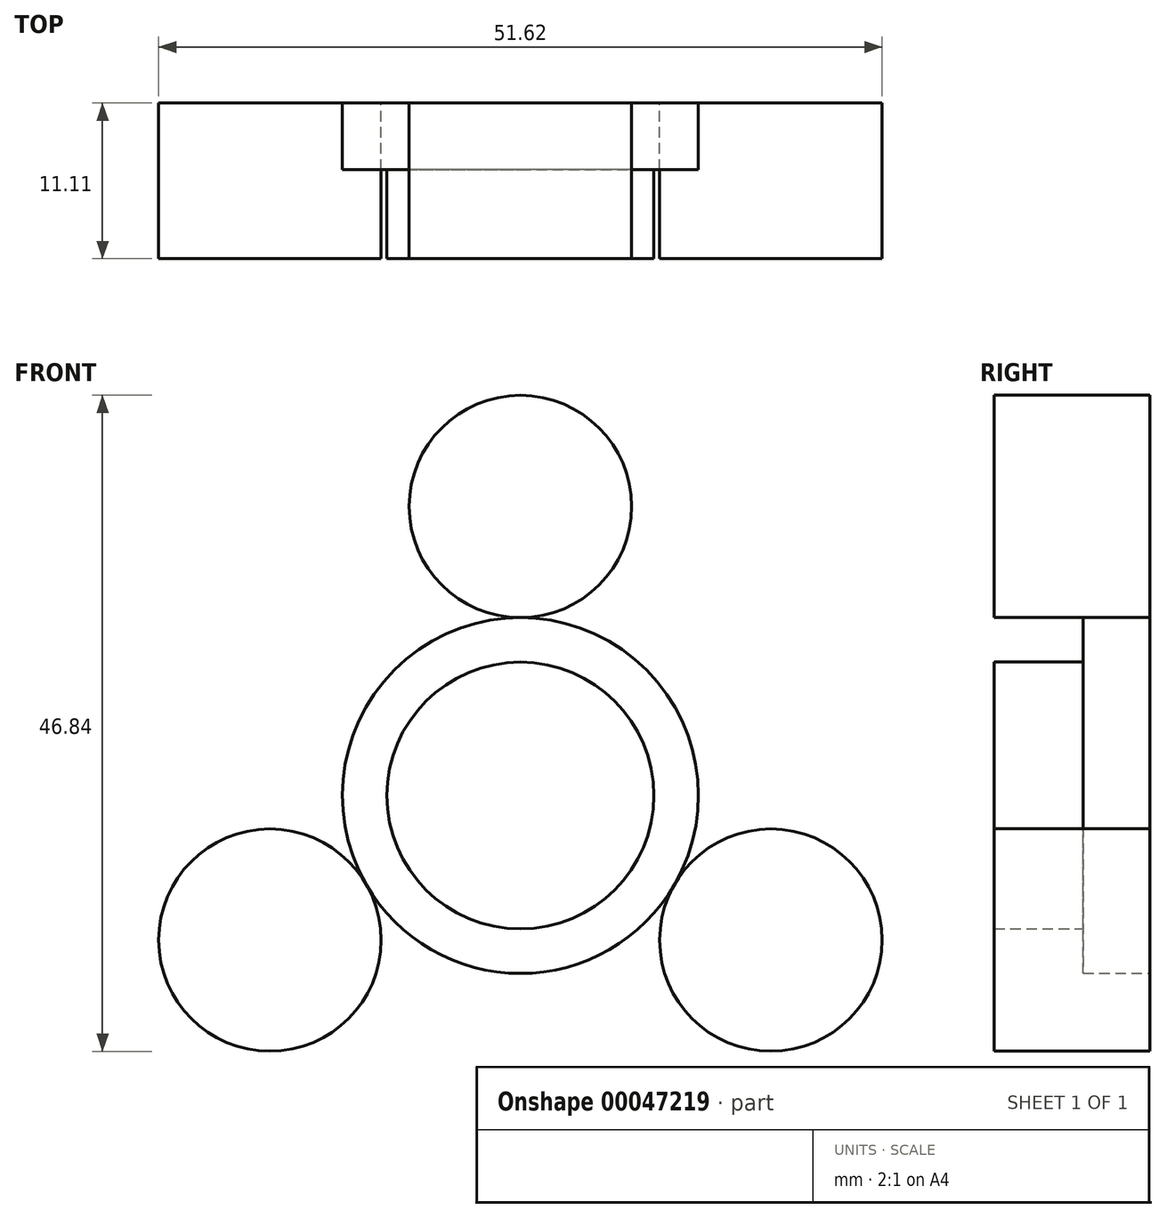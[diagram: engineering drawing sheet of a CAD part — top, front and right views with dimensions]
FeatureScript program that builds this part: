
annotation { "Feature Type Name" : "Feature", "Feature Type Description" : "" }
export const myFeature = defineFeature(function(context is Context, id is Id, definition is map)
    precondition{}
    {
        {
            var Q0;
            Q0=qCreatedBy(makeId("Front.planeOp"),FACE);
            var sketch = newSketch(context, id + "F0", { "sketchPlane" : qUnion([Q0])});
            skCircle(sketch, "E0", {"center": v(0, 0) * mm, "radius": 12.7 * mm});
            skCircle(sketch, "E1", {"center": v(0, 20.64) * mm, "radius": 7.94 * mm});
            skCircle(sketch, "E2.1.0", {"center": v(-17.87, -10.32) * mm, "radius": 7.94 * mm});
            skCircle(sketch, "E2.2.0", {"center": v(17.87, -10.32) * mm, "radius": 7.94 * mm});
            skCircle(sketch, "E3", {"center": v(0, 0) * mm, "radius": 28.58 * mm, "construction": true});
            skSolve(sketch);
        }
        {
            var Q0;
            Q0 = qSketchRegion(id + "F0", true);
            extrude(context, id + "F1", {"entities" : qUnion([Q0]), "depth" : 9.52 * mm / 2});
        }
        {
            var Q0;
            Q0=makeQuery(id+"F1.opExtrude","CAP_FACE",FACE,{"disambiguationData":[OSD([sQuery(id+"F0.wireOp",EDGE,"E0")])],"isStart":false});
            var sketch = newSketch(context, id + "F2", { "sketchPlane" : qUnion([Q0])});
            skCircle(sketch, "E4", {"center": v(0, 0) * mm, "radius": 9.53 * mm});
            skCircle(sketch, "E5.0", {"center": v(-17.87, -10.32) * mm, "radius": 7.94 * mm});
            skCircle(sketch, "E6.0", {"center": v(0, 20.64) * mm, "radius": 7.94 * mm});
            skCircle(sketch, "E7.0", {"center": v(17.87, -10.32) * mm, "radius": 7.94 * mm});
            skSolve(sketch);
        }
        {
            var Q0;
            Q0 = qSketchRegion(id + "F2", true);
            extrude(context, id + "F3", {"entities" : qUnion([Q0]), "operationType" : NewBodyOperationType.ADD, "depth" : 6.35 * mm});
        }
    });
